# Revit family: FireFighting_Hydrant-Valve-Support-Frame_Galvin_381384
name_source: partatom
category: Mechanical Equipment
revit_build: Autodesk Revit MEP 2012 (Build: 20110916_2132(x64)
units: mm (PartAtom-declared; Revit-internal decimal feet)

## types (1)
- 381384
    Assembly Code = D4030
    Description = Galvanised Dual Hydrant Valve Support Frame [WA]
    DimHeight = 980 mm  [stored 3.21522 ft]
    DimWidth = 500 mm  [stored 1.64042 ft]
    FilterObject_ANZRS = 381384
    Instructions = http://www.galvinengineering.com.au
    Keynote = 10520
    Manufacturer = Galvin Engineering
    Material = Metal_Fire-Fighting_Galvanised-Iron_15400
    Model = 381384
    ModifiedIssue_ANZRS = 20140514 $
    StyleOrType_ANZRS = Fire Fighting Equipment
    Type Comments = 381384
    URL = www.galvinengineering.com.au

note: [stored X ft] marks values corroborated as IEEE doubles in the binary element streams (Revit-internal decimal feet)

## geometry (parser evidence)
native form markers: Blend x2, Sweep x1
no freeform markers — native parametric forms only
